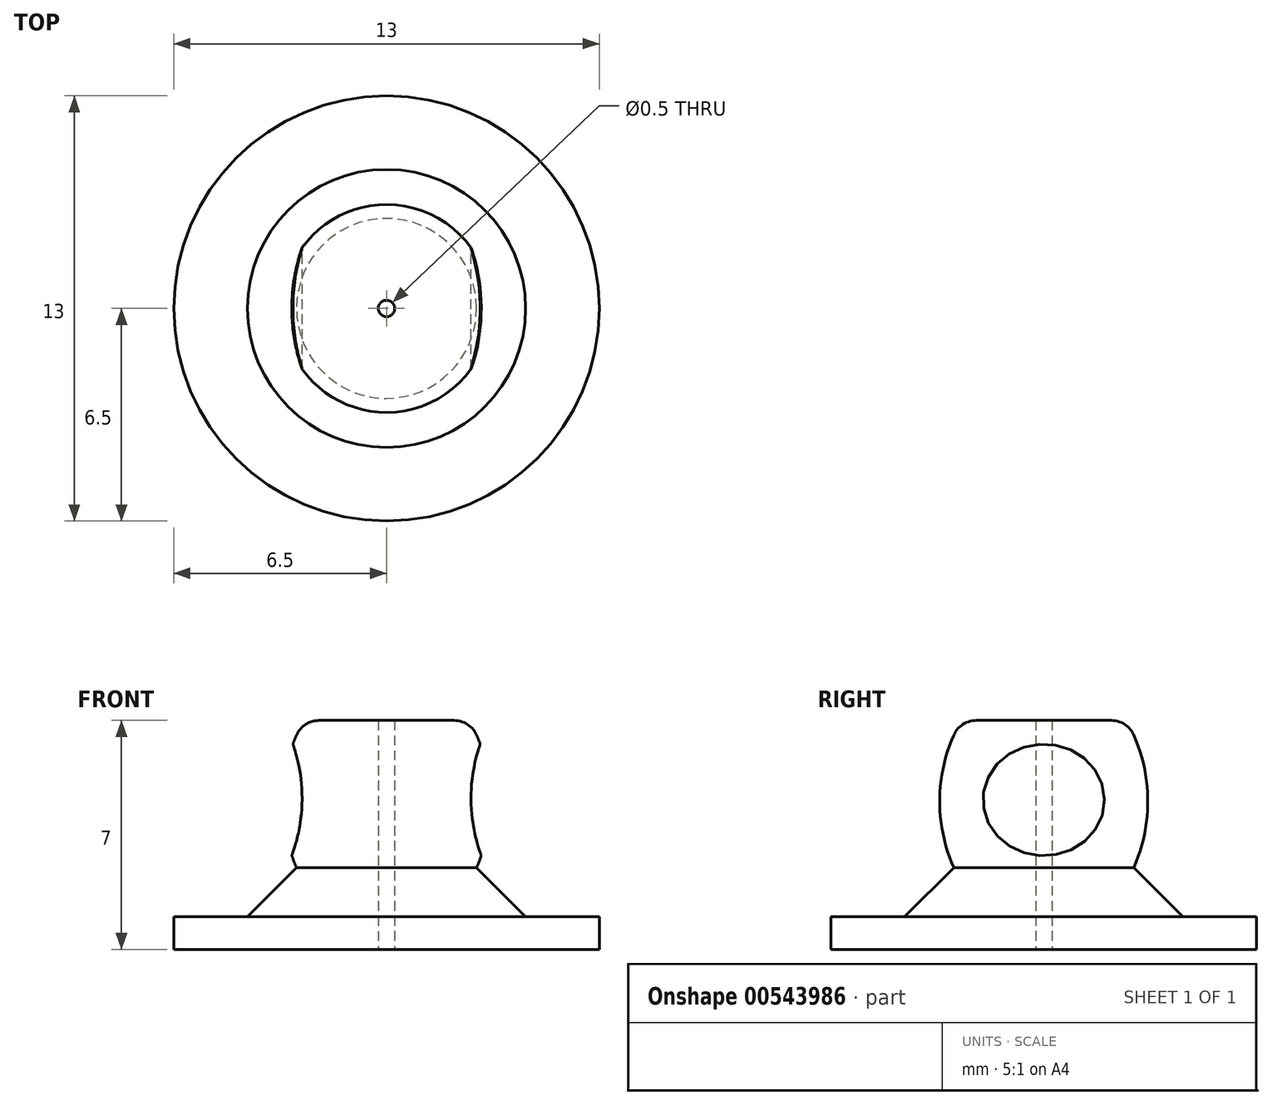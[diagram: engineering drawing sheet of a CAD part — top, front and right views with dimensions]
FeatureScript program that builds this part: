
annotation { "Feature Type Name" : "Feature", "Feature Type Description" : "" }
export const myFeature = defineFeature(function(context is Context, id is Id, definition is map)
    precondition{}
    {
        {
            var Q0;
            Q0=qCreatedBy(makeId("Front.planeOp"),FACE);
            var sketch = newSketch(context, id + "F0", { "sketchPlane" : qUnion([Q0])});
            skLineSegment(sketch, "E0", {"start": v(0.25, 0) * mm, "end": v(0.25, 7) * mm});
            skLineSegment(sketch, "E1", {"start": v(0, 0) * mm, "end": v(0, 8.8) * mm});
            skLineSegment(sketch, "E2", {"start": v(2.75, 2.5) * mm, "end": v(4.25, 1) * mm});
            skLineSegment(sketch, "E3", {"start": v(4.25, 1) * mm, "end": v(6.5, 1) * mm});
            skLineSegment(sketch, "E4", {"start": v(0.25, 0) * mm, "end": v(6.5, 0) * mm});
            skLineSegment(sketch, "E5", {"start": v(6.5, 0) * mm, "end": v(6.5, 1) * mm});
            skLineSegment(sketch, "E6", {"start": v(2.75, 2.5) * mm, "end": v(2.75, 1) * mm, "construction": true});
            skLineSegment(sketch, "E7", {"start": v(2.75, 1) * mm, "end": v(4.25, 1) * mm, "construction": true});
            skLineSegment(sketch, "E8", {"start": v(0.25, 7) * mm, "end": v(2.06, 7) * mm});
            skArc(sketch, "E9", {"start": v(2.75, 2.5) * mm, "mid": v(3.18, 4.53) * mm, "end": v(2.75, 6.55) * mm});
            skLineSegment(sketch, "E10", {"start": v(2.75, 2.5) * mm, "end": v(2.75, 6.55) * mm, "construction": true});
            skArc(sketch, "E11", {"start": v(2.06, 7) * mm, "mid": v(2.47, 6.88) * mm, "end": v(2.75, 6.55) * mm});
            skSolve(sketch);
        }
        {
            var Q0;
            Q0=makeQuery(id+"F0.imprint","IMPRINT",FACE,{"disambiguationData":[TD([[makeQuery(id+"F0.imprint","IMPRINT",EDGE,{"derivedFrom":sQuery(id+"F0.wireOp",EDGE,"E0")}),-1.0]])]});
            var Q1;
            Q1=sQuery(id+"F0.wireOp",EDGE,"E1");
            revolve(context, id + "F1", {"entities" : qUnion([Q0]), "axis" : qUnion([Q1]), "revolveType" : RevolveType.FULL});
        }
        {
            var Q0;
            Q0=qCreatedBy(makeId("Front.planeOp"),FACE);
            var sketch = newSketch(context, id + "F2", { "sketchPlane" : qUnion([Q0])});
            skArc(sketch, "E12", {"start": v(3.25, 7.12) * mm, "mid": v(2.58, 4.62) * mm, "end": v(3.25, 2.12) * mm});
            skLineSegment(sketch, "E13", {"start": v(3.25, 7.12) * mm, "end": v(3.25, 2.12) * mm, "construction": true});
            skLineSegment(sketch, "E14", {"start": v(3.25, 7.12) * mm, "end": v(4.25, 7.12) * mm});
            skLineSegment(sketch, "E15", {"start": v(4.25, 7.12) * mm, "end": v(4.25, 2.12) * mm});
            skLineSegment(sketch, "E16", {"start": v(4.25, 2.12) * mm, "end": v(3.25, 2.12) * mm});
            skSolve(sketch);
        }
        {
            var Q0;
            Q0 = qSketchRegion(id + "F2", true);
            extrude(context, id + "F3", {"entities" : qUnion([Q0]), "depth" : 5 * mm, "offsetDistance" : 25 * mm, "hasSecondDirection" : true, "secondDirectionOppositeDirection" : true, "secondDirectionDepth" : 5 * mm});
        }
        {
            var Q0;
            Q0=makeQuery(id+"F3.opExtrude","SWEPT_BODY",BODY,{"disambiguationData":[OSD([sQuery(id+"F2.wireOp",EDGE,"E12"),sQuery(id+"F2.wireOp",EDGE,"E14"),sQuery(id+"F2.wireOp",EDGE,"E15"),sQuery(id+"F2.wireOp",EDGE,"E16")])]});
            var Q1;
            Q1=qCreatedBy(makeId("Right.planeOp"),FACE);
            mirror(context, id + "F4", {"entities" : qUnion([Q0]), "mirrorPlane" : qUnion([Q1])});
        }
        {
            var Q0;
            Q0=makeQuery(id+"F3.opExtrude","SWEPT_BODY",BODY,{"disambiguationData":[OSD([sQuery(id+"F2.wireOp",EDGE,"E12"),sQuery(id+"F2.wireOp",EDGE,"E14"),sQuery(id+"F2.wireOp",EDGE,"E15"),sQuery(id+"F2.wireOp",EDGE,"E16")])]});
            var Q1;
            Q1=makeQuery(id+"F4.opPattern","COPY",BODY,{"derivedFrom":makeQuery(id+"F3.opExtrude","SWEPT_BODY",BODY,{"disambiguationData":[OSD([sQuery(id+"F2.wireOp",EDGE,"E12"),sQuery(id+"F2.wireOp",EDGE,"E14"),sQuery(id+"F2.wireOp",EDGE,"E15"),sQuery(id+"F2.wireOp",EDGE,"E16")])]}),"instanceName":"1"});
            var Q2;
            Q2=makeQuery(id+"F1.opRevolve","SWEPT_BODY",BODY,{"disambiguationData":[OSD([sQuery(id+"F0.wireOp",EDGE,"E0"),sQuery(id+"F0.wireOp",EDGE,"E2"),sQuery(id+"F0.wireOp",EDGE,"E3"),sQuery(id+"F0.wireOp",EDGE,"E4"),sQuery(id+"F0.wireOp",EDGE,"E5"),sQuery(id+"F0.wireOp",EDGE,"E8"),sQuery(id+"F0.wireOp",EDGE,"E9"),sQuery(id+"F0.wireOp",EDGE,"E11")])]});
            booleanBodies(context, id + "F5", {"operationType" : BooleanOperationType.SUBTRACTION, "tools" : qUnion([Q0, Q1]), "targets" : qUnion([Q2])});
        }
    });
